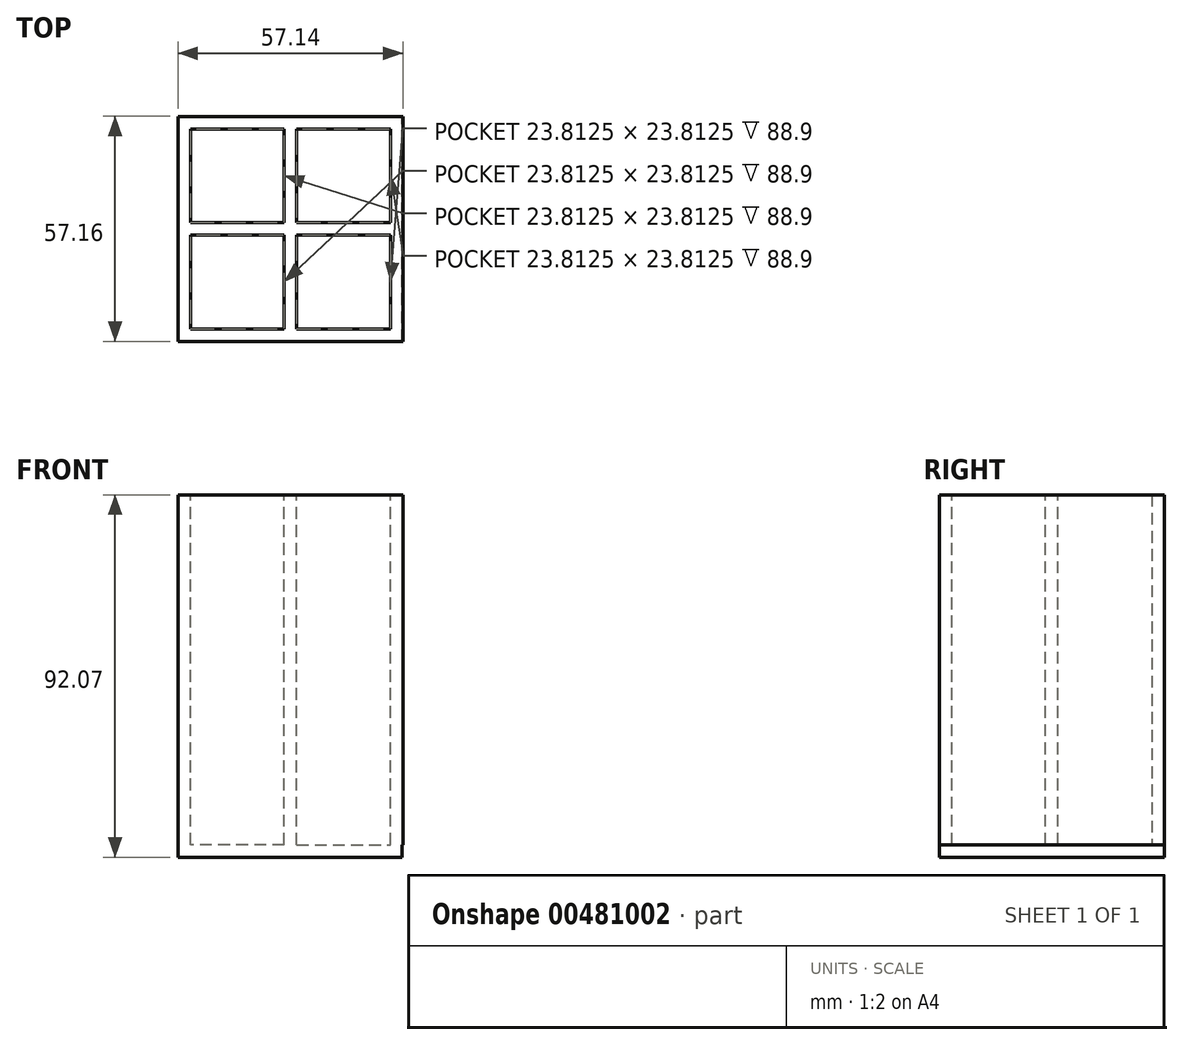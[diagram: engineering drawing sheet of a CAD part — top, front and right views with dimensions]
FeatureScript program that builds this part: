
annotation { "Feature Type Name" : "Feature", "Feature Type Description" : "" }
export const myFeature = defineFeature(function(context is Context, id is Id, definition is map)
    precondition{}
    {
        {
            var Q0;
            Q0=qCreatedBy(makeId("Front.planeOp"),FACE);
            var sketch = newSketch(context, id + "F0", { "sketchPlane" : qUnion([Q0])});
            skLineSegment(sketch, "E0.bottom", {"start": v(28.58, -44.45) * mm, "end": v(-28.57, -44.45) * mm});
            skLineSegment(sketch, "E0.top", {"start": v(28.57, 44.45) * mm, "end": v(-28.58, 44.45) * mm});
            skLineSegment(sketch, "E0.left", {"start": v(28.58, -44.45) * mm, "end": v(28.57, 44.45) * mm});
            skLineSegment(sketch, "E0.right", {"start": v(-28.57, -44.45) * mm, "end": v(-28.58, 44.45) * mm});
            skPoint(sketch, "E0.middle", {"position": v(0, 0) * mm});
            skSolve(sketch);
        }
        {
            var Q0;
            Q0 = qSketchRegion(id + "F0", true);
            extrude(context, id + "F1", {"entities" : qUnion([Q0]), "depth" : 3.17 * mm});
        }
        {
            var Q0;
            Q0=makeQuery(id+"F1.opExtrude","CAP_FACE",FACE,{"disambiguationData":[OSD([sQuery(id+"F0.wireOp",EDGE,"E0.bottom"),sQuery(id+"F0.wireOp",EDGE,"E0.top"),sQuery(id+"F0.wireOp",EDGE,"E0.left"),sQuery(id+"F0.wireOp",EDGE,"E0.right")])],"isStart":true});
            var sketch = newSketch(context, id + "F2", { "sketchPlane" : qUnion([Q0])});
            skLineSegment(sketch, "E1.bottom", {"start": v(-28.57, 44.45) * mm, "end": v(-25.4, 44.45) * mm});
            skLineSegment(sketch, "E1.top", {"start": v(-28.57, -44.45) * mm, "end": v(-25.4, -44.45) * mm});
            skLineSegment(sketch, "E1.left", {"start": v(-28.57, 44.45) * mm, "end": v(-28.57, -44.45) * mm});
            skLineSegment(sketch, "E1.right", {"start": v(-25.4, 44.45) * mm, "end": v(-25.4, -44.45) * mm});
            skSolve(sketch);
        }
        {
            var Q0;
            Q0 = qSketchRegion(id + "F2", true);
            extrude(context, id + "F3", {"entities" : qUnion([Q0]), "operationType" : NewBodyOperationType.ADD, "depth" : 50.8 * mm});
        }
        {
            var Q0;
            Q0=makeQuery(id+"F1.opExtrude","CAP_FACE",FACE,{"disambiguationData":[OSD([sQuery(id+"F0.wireOp",EDGE,"E0.bottom"),sQuery(id+"F0.wireOp",EDGE,"E0.top"),sQuery(id+"F0.wireOp",EDGE,"E0.left"),sQuery(id+"F0.wireOp",EDGE,"E0.right")])],"isStart":true});
            var sketch = newSketch(context, id + "F4", { "sketchPlane" : qUnion([Q0])});
            skLineSegment(sketch, "E2.bottom", {"start": v(28.58, 44.45) * mm, "end": v(25.4, 44.45) * mm});
            skLineSegment(sketch, "E2.top", {"start": v(28.58, -44.45) * mm, "end": v(25.4, -44.45) * mm});
            skLineSegment(sketch, "E2.left", {"start": v(28.58, 44.45) * mm, "end": v(28.58, -44.45) * mm});
            skLineSegment(sketch, "E2.right", {"start": v(25.4, 44.45) * mm, "end": v(25.4, -44.45) * mm});
            skSolve(sketch);
        }
        {
            var Q0;
            Q0 = qSketchRegion(id + "F4", true);
            extrude(context, id + "F5", {"entities" : qUnion([Q0]), "operationType" : NewBodyOperationType.ADD, "depth" : 50.8 * mm});
        }
        {
            var Q0;
            Q0=makeQuery(id+"F1.opExtrude","CAP_FACE",FACE,{"disambiguationData":[OSD([sQuery(id+"F0.wireOp",EDGE,"E0.bottom"),sQuery(id+"F0.wireOp",EDGE,"E0.top"),sQuery(id+"F0.wireOp",EDGE,"E0.left"),sQuery(id+"F0.wireOp",EDGE,"E0.right")])],"isStart":true});
            var sketch = newSketch(context, id + "F6", { "sketchPlane" : qUnion([Q0])});
            skLineSegment(sketch, "E3.bottom", {"start": v(1.59, -44.45) * mm, "end": v(-1.59, -44.45) * mm});
            skLineSegment(sketch, "E3.top", {"start": v(1.59, 44.45) * mm, "end": v(-1.59, 44.45) * mm});
            skLineSegment(sketch, "E3.left", {"start": v(1.59, -44.45) * mm, "end": v(1.59, 44.45) * mm});
            skLineSegment(sketch, "E3.right", {"start": v(-1.59, -44.45) * mm, "end": v(-1.59, 44.45) * mm});
            skPoint(sketch, "E3.middle", {"position": v(0, 0) * mm});
            skSolve(sketch);
        }
        {
            var Q0;
            Q0 = qSketchRegion(id + "F6", true);
            extrude(context, id + "F7", {"entities" : qUnion([Q0]), "operationType" : NewBodyOperationType.ADD, "depth" : 50.8 * mm});
        }
        {
            var Q0;
            Q0=makeQuery(id+"F7.opExtrude","CAP_FACE",FACE,{"disambiguationData":[OSD([sQuery(id+"F6.wireOp",EDGE,"E3.bottom"),sQuery(id+"F6.wireOp",EDGE,"E3.top"),sQuery(id+"F6.wireOp",EDGE,"E3.left"),sQuery(id+"F6.wireOp",EDGE,"E3.right")])],"isStart":false});
            extrude(context, id + "F8", {"entities" : qUnion([Q0]), "operationType" : NewBodyOperationType.REMOVE, "oppositeDirection" : true, "depth" : 50.8 * mm});
        }
        {
            var Q0;
            {var subQ0=sQuery(id+"F6.wireOp",EDGE,"E3.right");var subQ1=sQuery(id+"F6.wireOp",EDGE,"E3.left");var subQ2=sQuery(id+"F6.wireOp",EDGE,"E3.top");var subQ3=sQuery(id+"F6.wireOp",EDGE,"E3.bottom");var subQ6=sQuery(id+"F0.wireOp",EDGE,"E0.top");var subQ9=sQuery(id+"F0.wireOp",EDGE,"E0.bottom");var subQ14=makeQuery(id+"F1.opExtrude","CAP_FACE",FACE,{"disambiguationData":[OSD([subQ9,subQ6,sQuery(id+"F0.wireOp",EDGE,"E0.left"),sQuery(id+"F0.wireOp",EDGE,"E0.right")])],"isStart":true});Q0=makeQuery(id+"F8.boolean.opBoolean","MERGE",FACE,{"derivedFrom":[makeQuery(id+"F7.boolean.opBoolean","SPLIT",FACE,{"disambiguationData":[TD([makeQuery(id+"F3.opExtrude","SWEPT_FACE",FACE,{"disambiguationData":[OSD([sQuery(id+"F2.wireOp",EDGE,"E1.right")])]})])],"derivedFrom":subQ14}),makeQuery(id+"F7.boolean.opBoolean","SPLIT",FACE,{"disambiguationData":[TD([makeQuery(id+"F5.opExtrude","SWEPT_FACE",FACE,{"disambiguationData":[OSD([sQuery(id+"F4.wireOp",EDGE,"E2.right")])]})])],"derivedFrom":subQ14}),makeQuery(id+"F8.opExtrude","CAP_FACE",FACE,{"disambiguationData":[OSD([subQ3,subQ2,subQ1,subQ0])],"isStart":false})]});}
            var sketch = newSketch(context, id + "F9", { "sketchPlane" : qUnion([Q0])});
            skLineSegment(sketch, "E4.bottom", {"start": v(1.59, -44.45) * mm, "end": v(-1.59, -44.45) * mm});
            skLineSegment(sketch, "E4.top", {"start": v(1.59, 44.45) * mm, "end": v(-1.59, 44.45) * mm});
            skLineSegment(sketch, "E4.left", {"start": v(1.59, -44.45) * mm, "end": v(1.59, 44.45) * mm});
            skLineSegment(sketch, "E4.right", {"start": v(-1.59, -44.45) * mm, "end": v(-1.59, 44.45) * mm});
            skPoint(sketch, "E4.middle", {"position": v(0, 0) * mm});
            skSolve(sketch);
        }
        {
            var Q0;
            Q0=makeQuery(id+"F9.imprint","IMPRINT",FACE,{"disambiguationData":[TD([[makeQuery(id+"F9.imprint","IMPRINT",EDGE,{"derivedFrom":sQuery(id+"F9.wireOp",EDGE,"E4.bottom")}),1.0]])]});
            extrude(context, id + "F10", {"entities" : qUnion([Q0]), "operationType" : NewBodyOperationType.ADD, "depth" : 23.8 * mm});
        }
        {
            var Q0;
            Q0=makeQuery(id+"F10.opExtrude","CAP_FACE",FACE,{"disambiguationData":[OSD([sQuery(id+"F9.wireOp",EDGE,"E4.bottom"),sQuery(id+"F9.wireOp",EDGE,"E4.top"),sQuery(id+"F9.wireOp",EDGE,"E4.left"),sQuery(id+"F9.wireOp",EDGE,"E4.right")])],"isStart":false});
            var sketch = newSketch(context, id + "F11", { "sketchPlane" : qUnion([Q0])});
            skLineSegment(sketch, "E5.bottom", {"start": v(25.4, -44.45) * mm, "end": v(-25.4, -44.45) * mm});
            skLineSegment(sketch, "E5.top", {"start": v(25.4, 44.45) * mm, "end": v(-25.4, 44.45) * mm});
            skLineSegment(sketch, "E5.left", {"start": v(25.4, -44.45) * mm, "end": v(25.4, 44.45) * mm});
            skLineSegment(sketch, "E5.right", {"start": v(-25.4, -44.45) * mm, "end": v(-25.4, 44.45) * mm});
            skPoint(sketch, "E5.middle", {"position": v(0, 0) * mm});
            skSolve(sketch);
        }
        {
            var Q0;
            Q0 = qSketchRegion(id + "F11", true);
            extrude(context, id + "F12", {"entities" : qUnion([Q0]), "operationType" : NewBodyOperationType.ADD, "depth" : 3.17 * mm});
        }
        {
            var Q0;
            Q0=makeQuery(id+"F12.opExtrude","CAP_FACE",FACE,{"disambiguationData":[OSD([sQuery(id+"F11.wireOp",EDGE,"E5.bottom"),sQuery(id+"F11.wireOp",EDGE,"E5.top"),sQuery(id+"F11.wireOp",EDGE,"E5.left"),sQuery(id+"F11.wireOp",EDGE,"E5.right")])],"isStart":false});
            var sketch = newSketch(context, id + "F13", { "sketchPlane" : qUnion([Q0])});
            skLineSegment(sketch, "E6.bottom", {"start": v(1.59, -44.45) * mm, "end": v(-1.59, -44.45) * mm});
            skLineSegment(sketch, "E6.top", {"start": v(1.59, 44.45) * mm, "end": v(-1.59, 44.45) * mm});
            skLineSegment(sketch, "E6.left", {"start": v(1.59, -44.45) * mm, "end": v(1.59, 44.45) * mm});
            skLineSegment(sketch, "E6.right", {"start": v(-1.59, -44.45) * mm, "end": v(-1.59, 44.45) * mm});
            skPoint(sketch, "E6.middle", {"position": v(0, 0) * mm});
            skSolve(sketch);
        }
        {
            var Q0;
            Q0=makeQuery(id+"F13.imprint","IMPRINT",FACE,{"disambiguationData":[TD([[makeQuery(id+"F13.imprint","IMPRINT",EDGE,{"derivedFrom":sQuery(id+"F13.wireOp",EDGE,"E6.bottom")}),-1.0]])]});
            extrude(context, id + "F14", {"entities" : qUnion([Q0]), "operationType" : NewBodyOperationType.ADD, "depth" : 23.8 * mm});
        }
        {
            var Q0;
            Q0=makeQuery(id+"F14.opExtrude","CAP_FACE",FACE,{"disambiguationData":[OSD([sQuery(id+"F13.wireOp",EDGE,"E6.bottom"),sQuery(id+"F13.wireOp",EDGE,"E6.top"),sQuery(id+"F13.wireOp",EDGE,"E6.left"),sQuery(id+"F13.wireOp",EDGE,"E6.right")])],"isStart":false});
            var sketch = newSketch(context, id + "F15", { "sketchPlane" : qUnion([Q0])});
            skLineSegment(sketch, "E7.bottom", {"start": v(28.58, -44.45) * mm, "end": v(-28.57, -44.45) * mm});
            skLineSegment(sketch, "E7.top", {"start": v(28.57, 44.45) * mm, "end": v(-28.58, 44.45) * mm});
            skLineSegment(sketch, "E7.left", {"start": v(28.58, -44.45) * mm, "end": v(28.57, 44.45) * mm});
            skLineSegment(sketch, "E7.right", {"start": v(-28.57, -44.45) * mm, "end": v(-28.58, 44.45) * mm});
            skPoint(sketch, "E7.middle", {"position": v(0, 0) * mm});
            skSolve(sketch);
        }
        {
            var Q0;
            Q0 = qSketchRegion(id + "F15", true);
            extrude(context, id + "F16", {"entities" : qUnion([Q0]), "operationType" : NewBodyOperationType.ADD, "depth" : 3.17 * mm});
        }
        {
            var Q0;
            Q0=makeQuery(id+"F14.boolean.opBoolean","MERGE",FACE,{"derivedFrom":[makeQuery(id+"F12.boolean.opBoolean","MERGE",FACE,{"derivedFrom":[makeQuery(id+"F10.boolean.opBoolean","MERGE",FACE,{"derivedFrom":[makeQuery(id+"F7.boolean.opBoolean","MERGE",FACE,{"derivedFrom":[makeQuery(id+"F5.boolean.opBoolean","MERGE",FACE,{"derivedFrom":[makeQuery(id+"F3.boolean.opBoolean","MERGE",FACE,{"derivedFrom":[makeQuery(id+"F1.opExtrude","SWEPT_FACE",FACE,{"disambiguationData":[OSD([sQuery(id+"F0.wireOp",EDGE,"E0.bottom")])]}),makeQuery(id+"F3.opExtrude","SWEPT_FACE",FACE,{"disambiguationData":[OSD([sQuery(id+"F2.wireOp",EDGE,"E1.top")])]})]}),makeQuery(id+"F5.opExtrude","SWEPT_FACE",FACE,{"disambiguationData":[OSD([sQuery(id+"F4.wireOp",EDGE,"E2.top")])]})]}),makeQuery(id+"F7.opExtrude","SWEPT_FACE",FACE,{"disambiguationData":[OSD([sQuery(id+"F6.wireOp",EDGE,"E3.bottom")])]})]}),makeQuery(id+"F10.opExtrude","SWEPT_FACE",FACE,{"disambiguationData":[OSD([sQuery(id+"F9.wireOp",EDGE,"E4.bottom")])]})]}),makeQuery(id+"F12.opExtrude","SWEPT_FACE",FACE,{"disambiguationData":[OSD([sQuery(id+"F11.wireOp",EDGE,"E5.bottom")])]})]}),makeQuery(id+"F14.opExtrude","SWEPT_FACE",FACE,{"disambiguationData":[OSD([sQuery(id+"F13.wireOp",EDGE,"E6.bottom")])]})]});
            var sketch = newSketch(context, id + "F17", { "sketchPlane" : qUnion([Q0])});
            skLineSegment(sketch, "E8.bottom", {"start": v(-28.57, 3.18) * mm, "end": v(28.39, 3.18) * mm});
            skLineSegment(sketch, "E8.top", {"start": v(-28.57, -53.98) * mm, "end": v(28.39, -53.98) * mm});
            skLineSegment(sketch, "E8.left", {"start": v(-28.58, 3.17) * mm, "end": v(-28.58, -53.97) * mm});
            skLineSegment(sketch, "E8.right", {"start": v(28.39, 3.17) * mm, "end": v(28.39, -53.97) * mm});
            skSolve(sketch);
        }
        {
            var Q0;
            Q0 = qSketchRegion(id + "F17", true);
            extrude(context, id + "F18", {"entities" : qUnion([Q0]), "operationType" : NewBodyOperationType.ADD, "depth" : 3.17 * mm});
        }
    });
